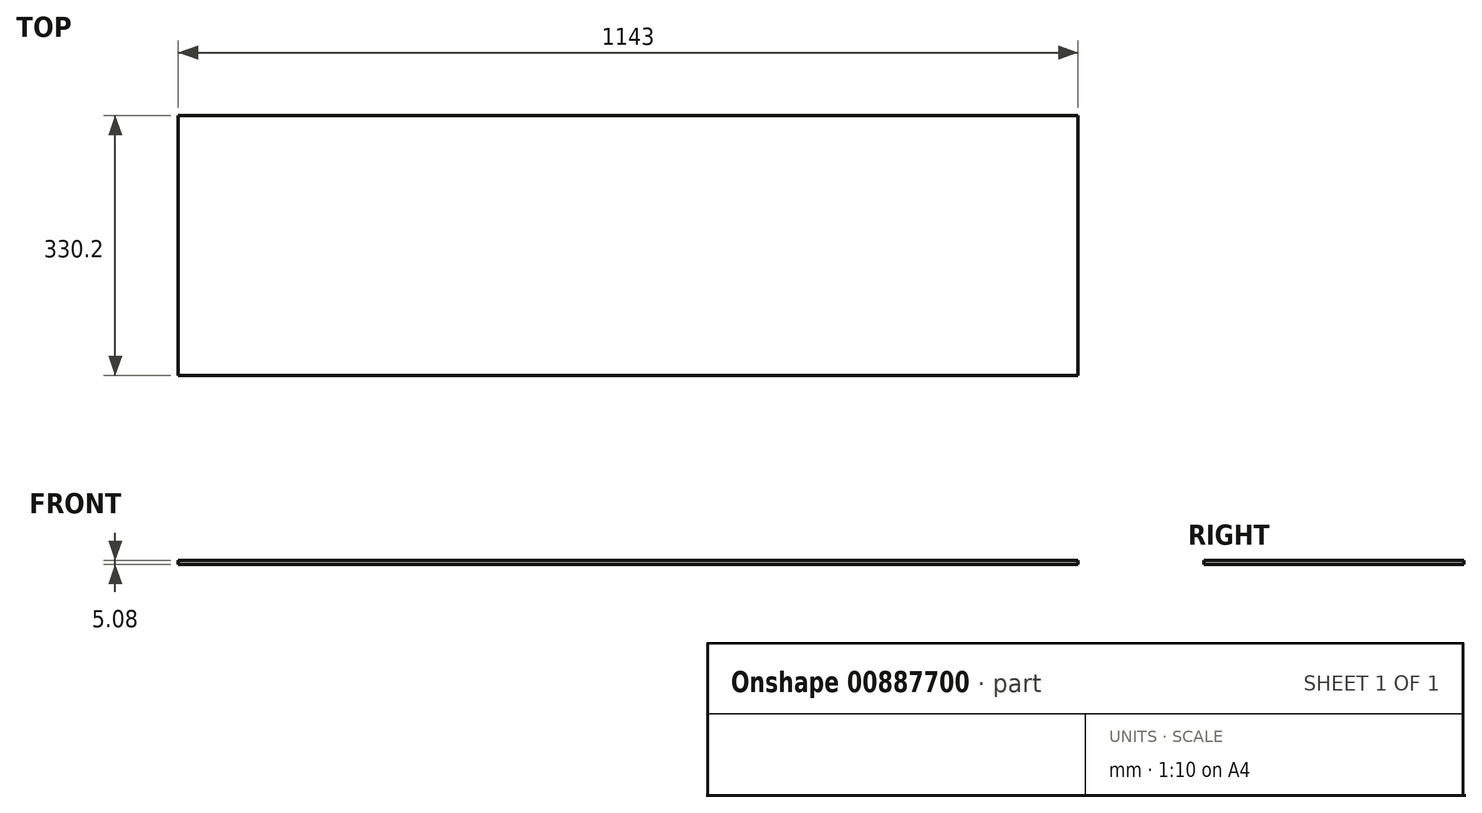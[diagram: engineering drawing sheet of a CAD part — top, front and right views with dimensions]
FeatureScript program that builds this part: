
annotation { "Feature Type Name" : "Feature", "Feature Type Description" : "" }
export const myFeature = defineFeature(function(context is Context, id is Id, definition is map)
    precondition{}
    {
        {
            var Q0;
            Q0=qCreatedBy(makeId("Top.planeOp"),FACE);
            var sketch = newSketch(context, id + "F0", { "sketchPlane" : qUnion([Q0])});
            skLineSegment(sketch, "E0.bottom", {"start": v(-612.05, -165.1) * mm, "end": v(530.95, -165.1) * mm});
            skLineSegment(sketch, "E0.top", {"start": v(-612.05, 165.1) * mm, "end": v(530.95, 165.1) * mm});
            skLineSegment(sketch, "E0.left", {"start": v(-612.05, -165.1) * mm, "end": v(-612.05, 165.1) * mm});
            skLineSegment(sketch, "E0.right", {"start": v(530.95, -165.1) * mm, "end": v(530.95, 165.1) * mm});
            skPoint(sketch, "E0.middle", {"position": v(-40.55, 0) * mm});
            skSolve(sketch);
        }
        {
            var Q0;
            Q0 = qSketchRegion(id + "F0", true);
            extrude(context, id + "F1", {"entities" : qUnion([Q0]), "depth" : 5.08 * mm, "offsetDistance" : 25.4 * mm});
        }
    });
